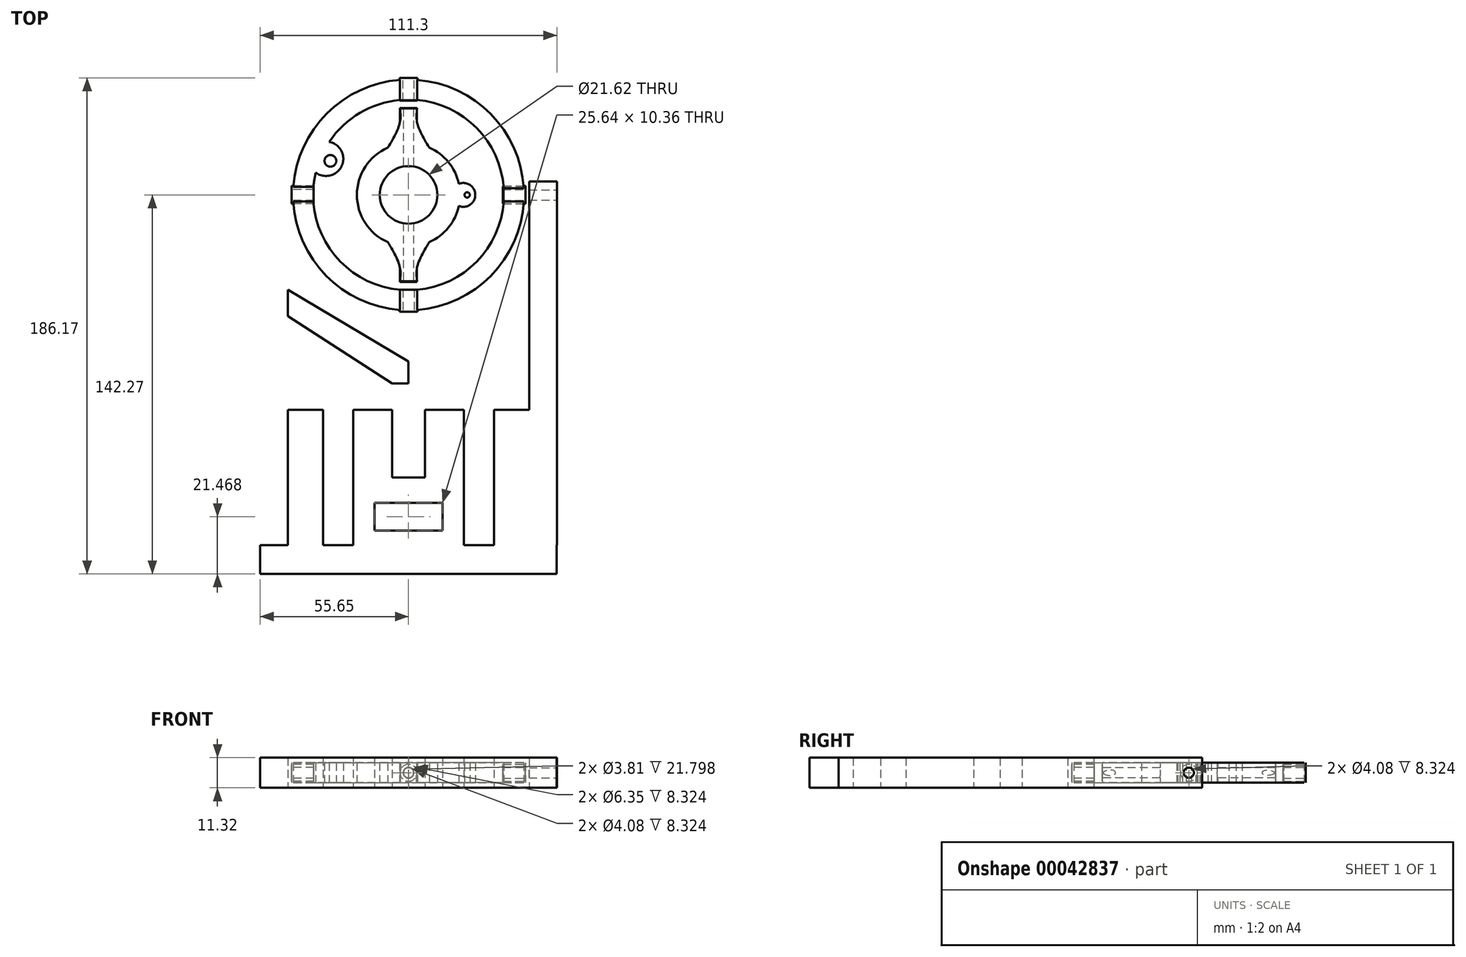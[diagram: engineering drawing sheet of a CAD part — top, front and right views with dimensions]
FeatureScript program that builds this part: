
annotation { "Feature Type Name" : "Feature", "Feature Type Description" : "" }
export const myFeature = defineFeature(function(context is Context, id is Id, definition is map)
    precondition{}
    {
        {
            var Q0;
            Q0=qCreatedBy(makeId("Top.planeOp"),FACE);
            var sketch = newSketch(context, id + "F0", { "sketchPlane" : qUnion([Q0])});
            skCircle(sketch, "E0", {"center": v(0, 0) * mm, "radius": 43.3 * mm});
            skCircle(sketch, "E1", {"center": v(0, 0) * mm, "radius": 35.8 * mm});
            skCircle(sketch, "E2", {"center": v(0, 0) * mm, "radius": 19.37 * mm});
            skCircle(sketch, "E3", {"center": v(0, 0) * mm, "radius": 10.81 * mm});
            skFitSpline(sketch, "E4", {"points": [v(-7.8, 17.73) * mm, v(-3.24, 27.17) * mm, v(-3.2, 32.44) * mm], "startDerivative": vector(10.8, 16.69) * mm, "endDerivative": vector(-0.96, 12.23) * mm});
            skFitSpline(sketch, "E5.MirrorCS", {"points": [v(7.8, 17.73) * mm, v(3.24, 27.17) * mm, v(3.2, 32.44) * mm], "startDerivative": vector(-10.8, 16.69) * mm, "endDerivative": vector(0.96, 12.23) * mm});
            skFitSpline(sketch, "E6.MirrorCS", {"points": [v(7.8, -17.73) * mm, v(3.24, -27.17) * mm, v(3.2, -32.44) * mm], "startDerivative": vector(-10.8, -16.69) * mm, "endDerivative": vector(0.96, -12.23) * mm});
            skFitSpline(sketch, "E7.MirrorCS", {"points": [v(-7.8, -17.73) * mm, v(-3.24, -27.17) * mm, v(-3.2, -32.44) * mm], "startDerivative": vector(10.8, -16.69) * mm, "endDerivative": vector(-0.96, -12.23) * mm});
            skLineSegment(sketch, "E8", {"start": v(-3.2, 32.44) * mm, "end": v(3.2, 32.44) * mm});
            skLineSegment(sketch, "E9", {"start": v(-3.2, -32.44) * mm, "end": v(3.2, -32.44) * mm});
            skArc(sketch, "E10", {"start": v(-34.8, 8.37) * mm, "mid": v(-25.03, 10.98) * mm, "end": v(-29.73, 19.93) * mm});
            skCircle(sketch, "E11", {"center": v(-29.31, 12.76) * mm, "radius": 2.2 * mm});
            skArc(sketch, "E12", {"start": v(18.92, -4.16) * mm, "mid": v(25.04, 0) * mm, "end": v(18.92, 4.16) * mm});
            skCircle(sketch, "E13", {"center": v(22, 0) * mm, "radius": 1 * mm});
            skLineSegment(sketch, "E14", {"start": v(3.2, 43.18) * mm, "end": v(3.2, 35.65) * mm});
            skLineSegment(sketch, "E15", {"start": v(-3.2, 43.18) * mm, "end": v(-3.2, 35.65) * mm});
            skLineSegment(sketch, "E16", {"start": v(-3.2, -35.65) * mm, "end": v(-3.2, -43.18) * mm});
            skLineSegment(sketch, "E17", {"start": v(3.2, -35.65) * mm, "end": v(3.2, -43.18) * mm});
            skLineSegment(sketch, "E18", {"start": v(35.7, 2.55) * mm, "end": v(43.22, 2.55) * mm});
            skLineSegment(sketch, "E19", {"start": v(-35.66, 3.06) * mm, "end": v(-43.18, 3.06) * mm});
            skLineSegment(sketch, "E20", {"start": v(-43.23, -2.4) * mm, "end": v(-35.71, -2.4) * mm});
            skLineSegment(sketch, "E21", {"start": v(35.71, -2.4) * mm, "end": v(43.23, -2.4) * mm});
            skSolve(sketch);
        }
        {
            var Q0;
            Q0=qCreatedBy(makeId("Front.planeOp"),FACE);
            var sketch = newSketch(context, id + "F1", { "sketchPlane" : qUnion([Q0])});
            skCircle(sketch, "E22", {"center": v(0, 0) * mm, "radius": 3.18 * mm});
            skCircle(sketch, "E23", {"center": v(0, 0) * mm, "radius": 2.03 * mm});
            skSolve(sketch);
        }
        {
            var Q0;
            Q0=makeQuery(id+"F1.imprint","IMPRINT",FACE,{"disambiguationData":[TD([[makeQuery(id+"F1.imprint","IMPRINT",EDGE,{"derivedFrom":sQuery(id+"F1.wireOp",EDGE,"E22")}),1.0]])]});
            extrude(context, id + "F2", {"entities" : qUnion([Q0]), "depth" : 19.43 * mm});
        }
        {
            var Q0;
            Q0=makeQuery(id+"F2.opExtrude","SWEPT_BODY",BODY,{"disambiguationData":[OSD([sQuery(id+"F1.wireOp",EDGE,"E22"),sQuery(id+"F1.wireOp",EDGE,"E23")])]});
            transform(context, id + "F3", {"entities" : qUnion([Q0]), "transformType" : TransformType.TRANSLATION_3D, "dx" : 0 * mm, "dy" : -11.62 * mm, "dz" : 0 * mm, "makeCopy" : false});
        }
        {
            var Q0;
            Q0=makeQuery(id+"F2.opExtrude","SWEPT_BODY",BODY,{"disambiguationData":[OSD([sQuery(id+"F1.wireOp",EDGE,"E22"),sQuery(id+"F1.wireOp",EDGE,"E23")])]});
            var Q1;
            Q1=sQuery(id+"F0.wireOp",EDGE,"E3");
            transform(context, id + "F4", {"entities" : qUnion([Q0]), "transformType" : TransformType.ROTATION, "transformAxis" : qUnion([Q1]), "angle" : 90 * degree, "makeCopy" : true});
        }
        {
            var Q0;
            Q0=makeQuery(id+"F4.opPattern","COPY",FACE,{"derivedFrom":makeQuery(id+"F2.opExtrude","CAP_FACE",FACE,{"disambiguationData":[OSD([sQuery(id+"F1.wireOp",EDGE,"E22"),sQuery(id+"F1.wireOp",EDGE,"E23")])],"isStart":false}),"instanceName":"1"});
            var sketch = newSketch(context, id + "F5", { "sketchPlane" : qUnion([Q0])});
            skCircle(sketch, "E24", {"center": v(0, 0) * mm, "radius": 2.04 * mm});
            skCircle(sketch, "E25", {"center": v(0, 0) * mm, "radius": 3.19 * mm});
            skSolve(sketch);
        }
        {
            var Q0;
            Q0=makeQuery(id+"F5.imprint","IMPRINT",FACE,{"disambiguationData":[TD([[makeQuery(id+"F5.imprint","IMPRINT",EDGE,{"derivedFrom":sQuery(id+"F5.wireOp",EDGE,"E24")}),-1.0]])]});
            extrude(context, id + "F6", {"entities" : qUnion([Q0]), "oppositeDirection" : true, "depth" : 8.32 * mm});
        }
        {
            var Q0;
            Q0=makeQuery(id+"F4.opPattern","COPY",BODY,{"derivedFrom":makeQuery(id+"F2.opExtrude","SWEPT_BODY",BODY,{"disambiguationData":[OSD([sQuery(id+"F1.wireOp",EDGE,"E22"),sQuery(id+"F1.wireOp",EDGE,"E23")])]}),"instanceName":"1"});
            deleteBodies(context, id + "F7", {"entities" : qUnion([Q0])});
        }
        {
            var Q0;
            Q0=makeQuery(id+"F6.opExtrude","SWEPT_BODY",BODY,{"disambiguationData":[OSD([sQuery(id+"F1.wireOp",EDGE,"E22"),sQuery(id+"F5.wireOp",EDGE,"E24")])]});
            var Q1;
            Q1=qCreatedBy(makeId("Right.planeOp"),FACE);
            mirror(context, id + "F8", {"entities" : qUnion([Q0]), "mirrorPlane" : qUnion([Q1])});
        }
        {
            var Q0;
            Q0=makeQuery(id+"F2.opExtrude","SWEPT_BODY",BODY,{"disambiguationData":[OSD([sQuery(id+"F1.wireOp",EDGE,"E22"),sQuery(id+"F1.wireOp",EDGE,"E23")])]});
            var Q1;
            Q1=qCreatedBy(makeId("Front.planeOp"),FACE);
            mirror(context, id + "F9", {"entities" : qUnion([Q0]), "mirrorPlane" : qUnion([Q1])});
        }
        {
            var Q0;
            Q0=makeQuery(id+"F8.opPattern","COPY",BODY,{"derivedFrom":makeQuery(id+"F6.opExtrude","SWEPT_BODY",BODY,{"disambiguationData":[OSD([sQuery(id+"F1.wireOp",EDGE,"E22"),sQuery(id+"F5.wireOp",EDGE,"E24")])]}),"instanceName":"1"});
            transform(context, id + "F10", {"entities" : qUnion([Q0]), "transformType" : TransformType.TRANSLATION_3D, "dx" : -12.85 * mm, "dy" : 0 * mm, "dz" : 0 * mm, "makeCopy" : false});
        }
        {
            var Q0;
            Q0=makeQuery(id+"F6.opExtrude","SWEPT_BODY",BODY,{"disambiguationData":[OSD([sQuery(id+"F1.wireOp",EDGE,"E22"),sQuery(id+"F5.wireOp",EDGE,"E24")])]});
            transform(context, id + "F11", {"entities" : qUnion([Q0]), "transformType" : TransformType.TRANSLATION_3D, "dx" : 12.67 * mm, "dy" : 0 * mm, "dz" : 0 * mm, "makeCopy" : false});
        }
        {
            var Q0;
            Q0=makeQuery(id+"F9.opPattern","COPY",BODY,{"derivedFrom":makeQuery(id+"F2.opExtrude","SWEPT_BODY",BODY,{"disambiguationData":[OSD([sQuery(id+"F1.wireOp",EDGE,"E22"),sQuery(id+"F1.wireOp",EDGE,"E23")])]}),"instanceName":"1"});
            transform(context, id + "F12", {"entities" : qUnion([Q0]), "transformType" : TransformType.TRANSLATION_3D, "dx" : 0 * mm, "dy" : 1.58 * mm, "dz" : 0 * mm, "makeCopy" : false});
        }
        {
            var Q0;
            Q0=makeQuery(id+"F2.opExtrude","SWEPT_BODY",BODY,{"disambiguationData":[OSD([sQuery(id+"F1.wireOp",EDGE,"E22"),sQuery(id+"F1.wireOp",EDGE,"E23")])]});
            transform(context, id + "F13", {"entities" : qUnion([Q0]), "transformType" : TransformType.TRANSLATION_3D, "dx" : 0 * mm, "dy" : -2.1 * mm, "dz" : 0 * mm, "makeCopy" : false});
        }
        {
            var Q0;
            Q0=makeQuery(id+"F8.opPattern","COPY",BODY,{"derivedFrom":makeQuery(id+"F6.opExtrude","SWEPT_BODY",BODY,{"disambiguationData":[OSD([sQuery(id+"F1.wireOp",EDGE,"E22"),sQuery(id+"F5.wireOp",EDGE,"E24")])]}),"instanceName":"1"});
            var Q1;
            Q1=makeQuery(id+"F6.opExtrude","SWEPT_BODY",BODY,{"disambiguationData":[OSD([sQuery(id+"F1.wireOp",EDGE,"E22"),sQuery(id+"F5.wireOp",EDGE,"E24")])]});
            var Q2;
            Q2=sQuery(id+"F0.wireOp",EDGE,"E3");
            transform(context, id + "F14", {"entities" : qUnion([Q0, Q1]), "transformType" : TransformType.ROTATION, "transformAxis" : qUnion([Q2]), "angle" : 90 * degree, "makeCopy" : true});
        }
        {
            var Q0;
            {var subQ2=sQuery(id+"F0.wireOp",EDGE,"E15");Q0=makeQuery(id+"F0.imprint","IMPRINT",FACE,{"disambiguationData":[TD([[makeQuery(id+"F0.imprint","IMPRINT",EDGE,{"derivedFrom":subQ2}),-1.0]])]});}
            var Q1;
            {var subQ2=sQuery(id+"F0.wireOp",EDGE,"E16");Q1=makeQuery(id+"F0.imprint","IMPRINT",FACE,{"disambiguationData":[TD([[makeQuery(id+"F0.imprint","IMPRINT",EDGE,{"derivedFrom":subQ2}),-1.0]])]});}
            var Q2;
            {var subQ1=sQuery(id+"F0.wireOp",EDGE,"E17");Q2=makeQuery(id+"F0.imprint","IMPRINT",FACE,{"disambiguationData":[TD([[makeQuery(id+"F0.imprint","IMPRINT",EDGE,{"derivedFrom":subQ1}),1.0]])]});}
            var Q3;
            {var subQ0=sQuery(id+"F0.wireOp",EDGE,"E14");Q3=makeQuery(id+"F0.imprint","IMPRINT",FACE,{"disambiguationData":[TD([[makeQuery(id+"F0.imprint","IMPRINT",EDGE,{"derivedFrom":subQ0}),1.0]])]});}
            var Q4;
            Q4=makeQuery(id+"F0.imprint","IMPRINT",FACE,{"disambiguationData":[TD([[makeQuery(id+"F0.imprint","IMPRINT",EDGE,{"derivedFrom":sQuery(id+"F0.wireOp",EDGE,"E3")}),-1.0]])]});
            var Q5;
            {var subQ0=sQuery(id+"F0.wireOp",EDGE,"E12");Q5=makeQuery(id+"F0.imprint","IMPRINT",FACE,{"disambiguationData":[TD([[makeQuery(id+"F0.imprint","IMPRINT",EDGE,{"derivedFrom":subQ0}),1.0]])]});}
            var Q6;
            {var subQ0=sQuery(id+"F0.wireOp",EDGE,"E10");Q6=makeQuery(id+"F0.imprint","IMPRINT",FACE,{"disambiguationData":[TD([[makeQuery(id+"F0.imprint","IMPRINT",EDGE,{"derivedFrom":subQ0}),1.0]])]});}
            var Q7;
            {var subQ1=sQuery(id+"F0.wireOp",EDGE,"E4");Q7=makeQuery(id+"F0.imprint","IMPRINT",FACE,{"disambiguationData":[TD([[makeQuery(id+"F0.imprint","IMPRINT",EDGE,{"derivedFrom":subQ1}),-1.0]])]});}
            var Q8;
            {var subQ1=sQuery(id+"F0.wireOp",EDGE,"E6.MirrorCS");Q8=makeQuery(id+"F0.imprint","IMPRINT",FACE,{"disambiguationData":[TD([[makeQuery(id+"F0.imprint","IMPRINT",EDGE,{"derivedFrom":subQ1}),-1.0]])]});}
            extrude(context, id + "F15", {"entities" : qUnion([Q0, Q1, Q2, Q3, Q4, Q5, Q6, Q7, Q8]), "endBound" : BoundingType.SYMMETRIC, "depth" : 7.5 * mm});
        }
        {
            var Q0;
            Q0=makeQuery(id+"F14.opPattern","COPY",FACE,{"derivedFrom":makeQuery(id+"F8.opPattern","COPY",FACE,{"derivedFrom":makeQuery(id+"F6.opExtrude","CAP_FACE",FACE,{"disambiguationData":[OSD([sQuery(id+"F1.wireOp",EDGE,"E22"),sQuery(id+"F5.wireOp",EDGE,"E24")])],"isStart":true}),"instanceName":"1"}),"instanceName":"1"});
            var sketch = newSketch(context, id + "F16", { "sketchPlane" : qUnion([Q0])});
            skLineSegment(sketch, "E26.bottom", {"start": v(-3.34, 3.73) * mm, "end": v(3.4, 3.73) * mm});
            skLineSegment(sketch, "E26.top", {"start": v(-3.34, -3.74) * mm, "end": v(3.4, -3.74) * mm});
            skLineSegment(sketch, "E26.left", {"start": v(-3.34, 3.73) * mm, "end": v(-3.34, -3.74) * mm});
            skLineSegment(sketch, "E26.right", {"start": v(3.4, 3.73) * mm, "end": v(3.4, -3.74) * mm});
            skCircle(sketch, "E27", {"center": v(0, 0) * mm, "radius": 3.14 * mm});
            skSolve(sketch);
        }
        {
            var Q0;
            Q0=makeQuery(id+"F16.imprint","IMPRINT",FACE,{"disambiguationData":[TD([[makeQuery(id+"F16.imprint","IMPRINT",EDGE,{"derivedFrom":sQuery(id+"F16.wireOp",EDGE,"E26.bottom")}),-1.0]])]});
            extrude(context, id + "F17", {"entities" : qUnion([Q0]), "oppositeDirection" : true, "depth" : 8.32 * mm});
        }
        {
            var Q0;
            Q0=makeQuery(id+"F17.opExtrude","SWEPT_BODY",BODY,{"disambiguationData":[OSD([sQuery(id+"F1.wireOp",EDGE,"E22"),sQuery(id+"F16.wireOp",EDGE,"E26.bottom"),sQuery(id+"F16.wireOp",EDGE,"E26.top"),sQuery(id+"F16.wireOp",EDGE,"E26.left"),sQuery(id+"F16.wireOp",EDGE,"E26.right")])]});
            var Q1;
            Q1=qCreatedBy(makeId("Front.planeOp"),FACE);
            mirror(context, id + "F18", {"entities" : qUnion([Q0]), "mirrorPlane" : qUnion([Q1])});
        }
        {
            var Q0;
            Q0=makeQuery(id+"F17.opExtrude","SWEPT_BODY",BODY,{"disambiguationData":[OSD([sQuery(id+"F1.wireOp",EDGE,"E22"),sQuery(id+"F16.wireOp",EDGE,"E26.bottom"),sQuery(id+"F16.wireOp",EDGE,"E26.top"),sQuery(id+"F16.wireOp",EDGE,"E26.left"),sQuery(id+"F16.wireOp",EDGE,"E26.right")])]});
            var Q1;
            Q1=makeQuery(id+"F18.opPattern","COPY",BODY,{"derivedFrom":makeQuery(id+"F17.opExtrude","SWEPT_BODY",BODY,{"disambiguationData":[OSD([sQuery(id+"F1.wireOp",EDGE,"E22"),sQuery(id+"F16.wireOp",EDGE,"E26.bottom"),sQuery(id+"F16.wireOp",EDGE,"E26.top"),sQuery(id+"F16.wireOp",EDGE,"E26.left"),sQuery(id+"F16.wireOp",EDGE,"E26.right")])]}),"instanceName":"1"});
            var Q2;
            Q2=sQuery(id+"F0.wireOp",EDGE,"E3");
            transform(context, id + "F19", {"entities" : qUnion([Q0, Q1]), "transformType" : TransformType.ROTATION, "transformAxis" : qUnion([Q2]), "angle" : 90 * degree, "makeCopy" : true});
        }
        {
            var Q0;
            Q0=makeQuery(id+"F2.opExtrude","SWEPT_BODY",BODY,{"disambiguationData":[OSD([sQuery(id+"F1.wireOp",EDGE,"E22"),sQuery(id+"F1.wireOp",EDGE,"E23")])]});
            transform(context, id + "F20", {"entities" : qUnion([Q0]), "transformType" : TransformType.TRANSLATION_3D, "dx" : 0 * mm, "dy" : 0.53 * mm, "dz" : 0 * mm, "makeCopy" : false});
        }
        {
            var Q0;
            Q0=makeQuery(id+"F2.opExtrude","SWEPT_BODY",BODY,{"disambiguationData":[OSD([sQuery(id+"F1.wireOp",EDGE,"E22"),sQuery(id+"F1.wireOp",EDGE,"E23")])]});
            var Q1;
            Q1=makeQuery(id+"F9.opPattern","COPY",BODY,{"derivedFrom":makeQuery(id+"F2.opExtrude","SWEPT_BODY",BODY,{"disambiguationData":[OSD([sQuery(id+"F1.wireOp",EDGE,"E22"),sQuery(id+"F1.wireOp",EDGE,"E23")])]}),"instanceName":"1"});
            var Q2;
            Q2=makeQuery(id+"F15.opExtrude","SWEPT_BODY",BODY,{"disambiguationData":[OSD([sQuery(id+"F0.wireOp",EDGE,"E2"),sQuery(id+"F0.wireOp",EDGE,"E3"),sQuery(id+"F0.wireOp",EDGE,"E4"),sQuery(id+"F0.wireOp",EDGE,"E5.MirrorCS"),sQuery(id+"F0.wireOp",EDGE,"E6.MirrorCS"),sQuery(id+"F0.wireOp",EDGE,"E7.MirrorCS"),sQuery(id+"F0.wireOp",EDGE,"E8"),sQuery(id+"F0.wireOp",EDGE,"E9"),sQuery(id+"F0.wireOp",EDGE,"E12"),sQuery(id+"F0.wireOp",EDGE,"E13")])]});
            booleanBodies(context, id + "F21", {"operationType" : BooleanOperationType.UNION, "tools" : qUnion([Q0, Q1, Q2])});
        }
        {
            var Q0;
            Q0=sQuery(id+"F1.wireOp",VERTEX,"E23.center");
            var Q1;
            Q1=makeQuery(id+"F2.opExtrude","SWEPT_BODY",BODY,{"disambiguationData":[OSD([sQuery(id+"F1.wireOp",EDGE,"E22"),sQuery(id+"F1.wireOp",EDGE,"E23")])]});
            hole(context, id + "F22", {"style" : HoleStyle.SIMPLE, "holeDiameter" : 3.8 * mm, "endStyle" : HoleEndStyle.THROUGH, "locations" : qUnion([Q0]), "scope" : qUnion([Q1])});
        }
        {
            var Q0;
            Q0=makeQuery(id+"F21.opBoolean","SPLIT",FACE,{"disambiguationData":[TD([makeQuery(id+"F2.opExtrude","SWEPT_FACE",FACE,{"disambiguationData":[OSD([sQuery(id+"F1.wireOp",EDGE,"E23")])]})])],"derivedFrom":makeQuery(id+"F15.opExtrude","SWEPT_FACE",FACE,{"disambiguationData":[OSD([sQuery(id+"F0.wireOp",EDGE,"E9")])]})});
            var sketch = newSketch(context, id + "F23", { "sketchPlane" : qUnion([Q0])});
            skCircle(sketch, "E28", {"center": v(0, 0) * mm, "radius": 1.92 * mm});
            skSolve(sketch);
        }
        {
            var Q0;
            Q0=sQuery(id+"F23.wireOp",VERTEX,"E28.center");
            var Q1;
            Q1=makeQuery(id+"F2.opExtrude","SWEPT_BODY",BODY,{"disambiguationData":[OSD([sQuery(id+"F1.wireOp",EDGE,"E22"),sQuery(id+"F1.wireOp",EDGE,"E23")])]});
            hole(context, id + "F24", {"style" : HoleStyle.SIMPLE, "holeDiameter" : 3.8 * mm, "endStyle" : HoleEndStyle.THROUGH, "locations" : qUnion([Q0]), "scope" : qUnion([Q1])});
        }
        {
            var Q0;
            Q0=qCreatedBy(makeId("Top.planeOp"),FACE);
            var sketch = newSketch(context, id + "F25", { "sketchPlane" : qUnion([Q0])});
            skLineSegment(sketch, "E29.bottom", {"start": v(-64.32, 5) * mm, "end": v(0, 5) * mm});
            skLineSegment(sketch, "E29.top", {"start": v(-64.32, -131.44) * mm, "end": v(0, -131.44) * mm});
            skLineSegment(sketch, "E29.left", {"start": v(-64.32, 5) * mm, "end": v(-64.32, -131.44) * mm});
            skLineSegment(sketch, "E29.right", {"start": v(0, 5) * mm, "end": v(0, -131.44) * mm});
            skLineSegment(sketch, "E30", {"start": v(-45.25, 5) * mm, "end": v(-45.25, -131.44) * mm});
            skLineSegment(sketch, "E31", {"start": v(-45.25, -35.63) * mm, "end": v(0, -62.57) * mm});
            skLineSegment(sketch, "E32", {"start": v(0, -62.57) * mm, "end": v(0, -69.89) * mm});
            skLineSegment(sketch, "E33.bottom", {"start": v(-45.25, -70.79) * mm, "end": v(0, -70.79) * mm});
            skLineSegment(sketch, "E33.top", {"start": v(-45.25, -80.7) * mm, "end": v(0, -80.7) * mm});
            skLineSegment(sketch, "E33.left", {"start": v(-45.25, -70.79) * mm, "end": v(-45.25, -80.7) * mm});
            skLineSegment(sketch, "E33.right", {"start": v(0, -70.79) * mm, "end": v(0, -80.7) * mm});
            skLineSegment(sketch, "E34.bottom", {"start": v(0, -80.7) * mm, "end": v(-6.14, -80.7) * mm});
            skLineSegment(sketch, "E34.top", {"start": v(0, -106.1) * mm, "end": v(-6.14, -106.1) * mm});
            skLineSegment(sketch, "E34.left", {"start": v(0, -80.7) * mm, "end": v(0, -106.1) * mm});
            skLineSegment(sketch, "E34.right", {"start": v(-6.14, -80.7) * mm, "end": v(-6.14, -106.1) * mm});
            skLineSegment(sketch, "E35.bottom", {"start": v(0, -115.62) * mm, "end": v(-12.82, -115.62) * mm});
            skLineSegment(sketch, "E35.top", {"start": v(0, -125.98) * mm, "end": v(-12.82, -125.98) * mm});
            skLineSegment(sketch, "E35.left", {"start": v(0, -115.62) * mm, "end": v(0, -125.98) * mm});
            skLineSegment(sketch, "E35.right", {"start": v(-12.82, -115.62) * mm, "end": v(-12.82, -125.98) * mm});
            skLineSegment(sketch, "E36", {"start": v(-20.76, -80.7) * mm, "end": v(-20.76, -131.44) * mm});
            skLineSegment(sketch, "E37", {"start": v(-20.76, -131.44) * mm, "end": v(-32.06, -131.44) * mm});
            skLineSegment(sketch, "E38", {"start": v(-32.06, -131.44) * mm, "end": v(-32.06, -80.7) * mm});
            skLineSegment(sketch, "E39.MirrorCS", {"start": v(64.32, 5) * mm, "end": v(0, 5) * mm});
            skLineSegment(sketch, "E40.MirrorCS", {"start": v(64.32, -131.44) * mm, "end": v(0, -131.44) * mm});
            skLineSegment(sketch, "E41.MirrorCS", {"start": v(0, -125.98) * mm, "end": v(12.82, -125.98) * mm});
            skLineSegment(sketch, "E42.MirrorCS", {"start": v(12.82, -115.62) * mm, "end": v(12.82, -125.98) * mm});
            skLineSegment(sketch, "E43.MirrorCS", {"start": v(0, -115.62) * mm, "end": v(12.82, -115.62) * mm});
            skLineSegment(sketch, "E44.MirrorCS", {"start": v(0, -106.1) * mm, "end": v(6.14, -106.1) * mm});
            skLineSegment(sketch, "E45.MirrorCS", {"start": v(6.14, -80.7) * mm, "end": v(6.14, -106.1) * mm});
            skLineSegment(sketch, "E46.MirrorCS", {"start": v(20.76, -80.7) * mm, "end": v(20.76, -131.44) * mm});
            skLineSegment(sketch, "E47.MirrorCS", {"start": v(32.06, -131.44) * mm, "end": v(32.06, -80.7) * mm});
            skLineSegment(sketch, "E48.MirrorCS", {"start": v(45.25, -80.7) * mm, "end": v(0, -80.7) * mm});
            skLineSegment(sketch, "E49.MirrorCS", {"start": v(45.25, -70.79) * mm, "end": v(0, -70.79) * mm});
            skLineSegment(sketch, "E50.MirrorCS", {"start": v(45.25, -35.63) * mm, "end": v(0, -62.57) * mm});
            skLineSegment(sketch, "E51.MirrorCS", {"start": v(64.32, 5) * mm, "end": v(64.32, -131.44) * mm});
            skLineSegment(sketch, "E52.MirrorCS", {"start": v(45.25, 5) * mm, "end": v(45.25, -131.44) * mm});
            skLineSegment(sketch, "E53", {"start": v(-55.65, 5) * mm, "end": v(-55.65, -131.44) * mm});
            skLineSegment(sketch, "E54.MirrorCS", {"start": v(55.65, 5) * mm, "end": v(55.65, -131.44) * mm});
            skLineSegment(sketch, "E55", {"start": v(-45.25, -45.45) * mm, "end": v(-6.12, -70.79) * mm});
            skLineSegment(sketch, "E56.MirrorCS", {"start": v(45.25, -45.45) * mm, "end": v(6.12, -70.79) * mm});
            skLineSegment(sketch, "E57.bottom", {"start": v(-55.65, -131.44) * mm, "end": v(55.56, -131.44) * mm});
            skLineSegment(sketch, "E57.top", {"start": v(-55.65, -142.27) * mm, "end": v(55.56, -142.27) * mm});
            skLineSegment(sketch, "E57.left", {"start": v(-55.65, -131.44) * mm, "end": v(-55.65, -142.27) * mm});
            skLineSegment(sketch, "E57.right", {"start": v(55.56, -131.44) * mm, "end": v(55.56, -142.27) * mm});
            skSolve(sketch);
        }
        {
            var Q0;
            {var subQ4=sQuery(id+"F25.wireOp",EDGE,"E33.left");Q0=makeQuery(id+"F25.imprint","IMPRINT",FACE,{"disambiguationData":[TD([[makeQuery(id+"F25.imprint","IMPRINT",EDGE,{"derivedFrom":subQ4}),-1.0]])]});}
            var Q1;
            {var subQ6=sQuery(id+"F25.wireOp",EDGE,"E31");Q1=makeQuery(id+"F25.imprint","IMPRINT",FACE,{"disambiguationData":[TD([[makeQuery(id+"F25.imprint","IMPRINT",EDGE,{"derivedFrom":subQ6}),-1.0]])]});}
            var Q2;
            {var subQ6=sQuery(id+"F25.wireOp",EDGE,"E32");Q2=makeQuery(id+"F25.imprint","IMPRINT",FACE,{"disambiguationData":[TD([[makeQuery(id+"F25.imprint","IMPRINT",EDGE,{"derivedFrom":subQ6}),1.0]])]});}
            var Q3;
            {var subQ5=sQuery(id+"F25.wireOp",EDGE,"E54.MirrorCS");Q3=makeQuery(id+"F25.imprint","IMPRINT",FACE,{"disambiguationData":[TD([[makeQuery(id+"F25.imprint","IMPRINT",EDGE,{"derivedFrom":subQ5}),-1.0]])]});}
            var Q4;
            {var subQ7=sQuery(id+"F25.wireOp",EDGE,"E33.right");Q4=makeQuery(id+"F25.imprint","IMPRINT",FACE,{"disambiguationData":[TD([[makeQuery(id+"F25.imprint","IMPRINT",EDGE,{"derivedFrom":subQ7}),1.0]])]});}
            var Q5;
            {var subQ2=sQuery(id+"F25.wireOp",EDGE,"E33.left");Q5=makeQuery(id+"F25.imprint","IMPRINT",FACE,{"disambiguationData":[TD([[makeQuery(id+"F25.imprint","IMPRINT",EDGE,{"derivedFrom":subQ2}),1.0]])]});}
            var Q6;
            Q6=makeQuery(id+"F25.imprint","IMPRINT",FACE,{"disambiguationData":[TD([[makeQuery(id+"F25.imprint","IMPRINT",EDGE,{"derivedFrom":sQuery(id+"F25.wireOp",EDGE,"E57.top")}),1.0]])]});
            var Q7;
            {var subQ1=sQuery(id+"F25.wireOp",EDGE,"E38");Q7=makeQuery(id+"F25.imprint","IMPRINT",FACE,{"disambiguationData":[TD([[makeQuery(id+"F25.imprint","IMPRINT",EDGE,{"derivedFrom":subQ1}),1.0]])]});}
            var Q8;
            {var subQ8=sQuery(id+"F25.wireOp",EDGE,"E34.top");Q8=makeQuery(id+"F25.imprint","IMPRINT",FACE,{"disambiguationData":[TD([[makeQuery(id+"F25.imprint","IMPRINT",EDGE,{"derivedFrom":subQ8}),1.0]])]});}
            var Q9;
            {var subQ9=sQuery(id+"F25.wireOp",EDGE,"E41.MirrorCS");Q9=makeQuery(id+"F25.imprint","IMPRINT",FACE,{"disambiguationData":[TD([[makeQuery(id+"F25.imprint","IMPRINT",EDGE,{"derivedFrom":subQ9}),-1.0]])]});}
            var Q10;
            {var subQ3=sQuery(id+"F25.wireOp",EDGE,"E47.MirrorCS");Q10=makeQuery(id+"F25.imprint","IMPRINT",FACE,{"disambiguationData":[TD([[makeQuery(id+"F25.imprint","IMPRINT",EDGE,{"derivedFrom":subQ3}),-1.0]])]});}
            extrude(context, id + "F26", {"entities" : qUnion([Q0, Q1, Q2, Q3, Q4, Q5, Q6, Q7, Q8, Q9, Q10]), "endBound" : BoundingType.SYMMETRIC, "depth" : 11.32 * mm});
        }
        {
            var Q0;
            Q0=makeQuery(id+"F26.opExtrude","SWEPT_FACE",FACE,{"disambiguationData":[OSD([sQuery(id+"F25.wireOp",EDGE,"E54.MirrorCS")])]});
            var sketch = newSketch(context, id + "F27", { "sketchPlane" : qUnion([Q0])});
            skCircle(sketch, "E58", {"center": v(0, 0) * mm, "radius": 1.88 * mm});
            skSolve(sketch);
        }
        {
            var Q0;
            Q0=sQuery(id+"F27.wireOp",VERTEX,"E58.center");
            var Q1;
            Q1=makeQuery(id+"F26.opExtrude","SWEPT_BODY",BODY,{"disambiguationData":[OSD([sQuery(id+"F25.wireOp",EDGE,"E29.bottom"),sQuery(id+"F25.wireOp",EDGE,"E30"),sQuery(id+"F25.wireOp",EDGE,"E31"),sQuery(id+"F25.wireOp",EDGE,"E33.bottom"),sQuery(id+"F25.wireOp",EDGE,"E33.top"),sQuery(id+"F25.wireOp",EDGE,"E34.bottom"),sQuery(id+"F25.wireOp",EDGE,"E34.top"),sQuery(id+"F25.wireOp",EDGE,"E34.right"),sQuery(id+"F25.wireOp",EDGE,"E35.bottom"),sQuery(id+"F25.wireOp",EDGE,"E35.top"),sQuery(id+"F25.wireOp",EDGE,"E35.right"),sQuery(id+"F25.wireOp",EDGE,"E36"),sQuery(id+"F25.wireOp",EDGE,"E38"),sQuery(id+"F25.wireOp",EDGE,"E39.MirrorCS"),sQuery(id+"F25.wireOp",EDGE,"E40.MirrorCS"),sQuery(id+"F25.wireOp",EDGE,"E41.MirrorCS"),sQuery(id+"F25.wireOp",EDGE,"E42.MirrorCS"),sQuery(id+"F25.wireOp",EDGE,"E43.MirrorCS"),sQuery(id+"F25.wireOp",EDGE,"E44.MirrorCS"),sQuery(id+"F25.wireOp",EDGE,"E45.MirrorCS"),sQuery(id+"F25.wireOp",EDGE,"E46.MirrorCS"),sQuery(id+"F25.wireOp",EDGE,"E47.MirrorCS"),sQuery(id+"F25.wireOp",EDGE,"E48.MirrorCS"),sQuery(id+"F25.wireOp",EDGE,"E49.MirrorCS"),sQuery(id+"F25.wireOp",EDGE,"E50.MirrorCS"),sQuery(id+"F25.wireOp",EDGE,"E52.MirrorCS"),sQuery(id+"F25.wireOp",EDGE,"E53"),sQuery(id+"F25.wireOp",EDGE,"E54.MirrorCS"),sQuery(id+"F25.wireOp",EDGE,"E55"),sQuery(id+"F25.wireOp",EDGE,"E56.MirrorCS"),sQuery(id+"F25.wireOp",EDGE,"E57.bottom"),sQuery(id+"F25.wireOp",EDGE,"E57.top"),sQuery(id+"F25.wireOp",EDGE,"E57.left"),sQuery(id+"F25.wireOp",EDGE,"E57.right")])]});
            hole(context, id + "F28", {"style" : HoleStyle.SIMPLE, "holeDiameter" : 3.8 * mm, "endStyle" : HoleEndStyle.THROUGH, "locations" : qUnion([Q0]), "scope" : qUnion([Q1])});
        }
    });
